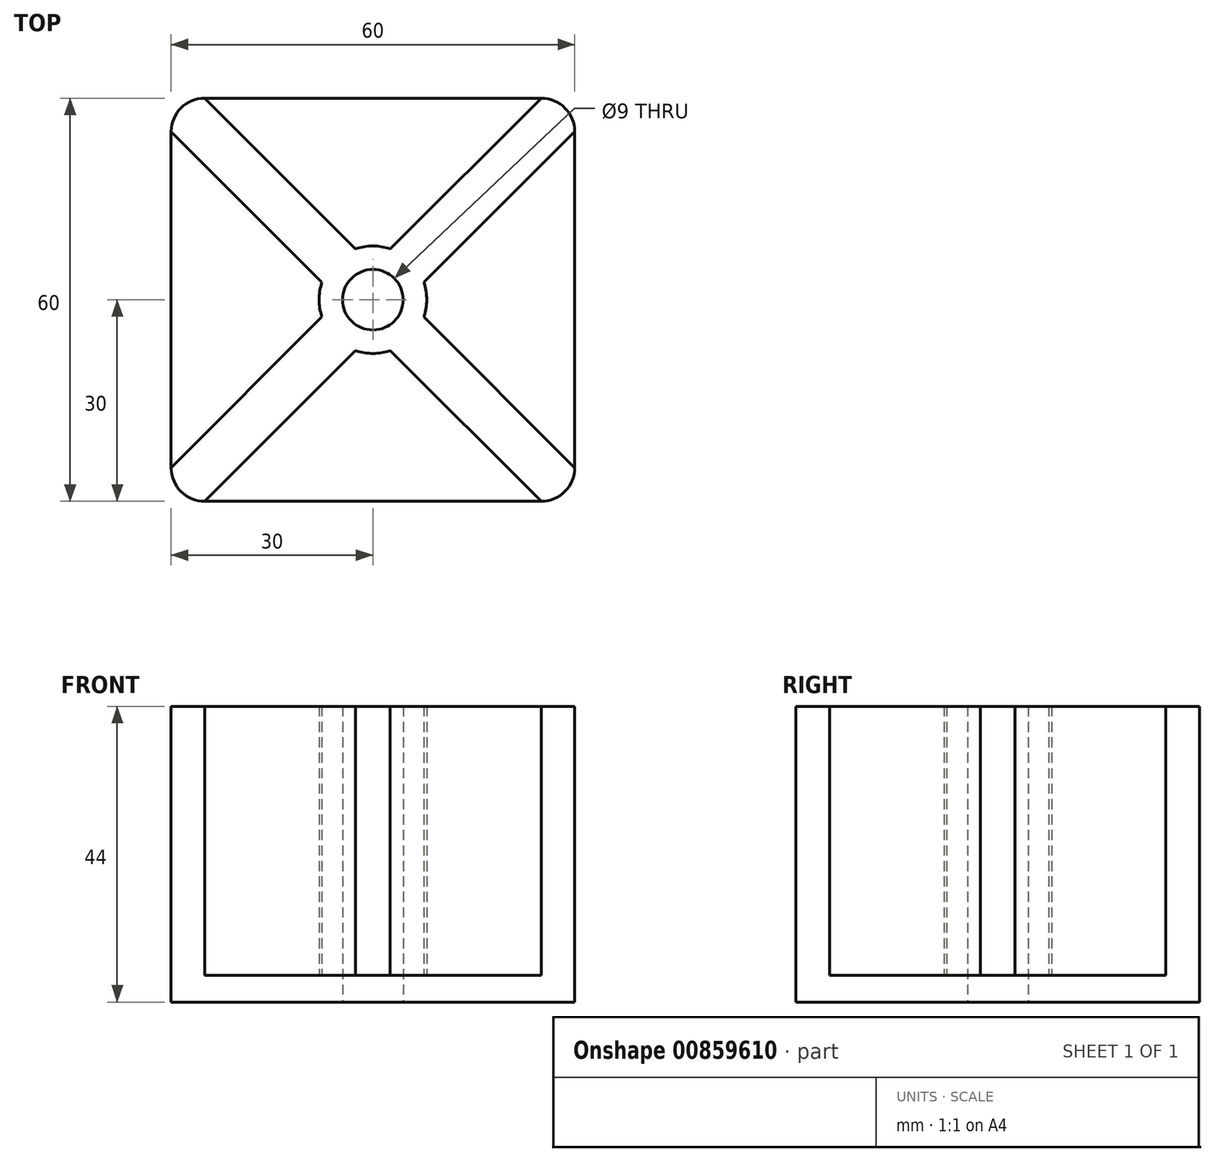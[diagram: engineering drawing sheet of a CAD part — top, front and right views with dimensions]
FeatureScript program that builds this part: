
annotation { "Feature Type Name" : "Feature", "Feature Type Description" : "" }
export const myFeature = defineFeature(function(context is Context, id is Id, definition is map)
    precondition{}
    {
        {
            var Q0;
            Q0=qCreatedBy(makeId("Top.planeOp"),FACE);
            var sketch = newSketch(context, id + "F0", { "sketchPlane" : qUnion([Q0])});
            skLineSegment(sketch, "E0.bottom", {"start": v(25, -30) * mm, "end": v(-25, -30) * mm});
            skLineSegment(sketch, "E0.top", {"start": v(25, 30) * mm, "end": v(-25, 30) * mm});
            skLineSegment(sketch, "E0.left", {"start": v(30, -25) * mm, "end": v(30, 25) * mm});
            skLineSegment(sketch, "E0.right", {"start": v(-30, -25) * mm, "end": v(-30, 25) * mm});
            skPoint(sketch, "E0.middle", {"position": v(0, 0) * mm});
            skPoint(sketch, "E1.visualSharp", {"position": v(30, 30) * mm});
            skArc(sketch, "E1.filletArc", {"start": v(30, 25) * mm, "mid": v(28.54, 28.54) * mm, "end": v(25, 30) * mm});
            skPoint(sketch, "E2.visualSharp", {"position": v(-30, 30) * mm});
            skArc(sketch, "E2.filletArc", {"start": v(-25, 30) * mm, "mid": v(-28.54, 28.54) * mm, "end": v(-30, 25) * mm});
            skPoint(sketch, "E3.visualSharp", {"position": v(-30, -30) * mm});
            skArc(sketch, "E3.filletArc", {"start": v(-30, -25) * mm, "mid": v(-28.54, -28.54) * mm, "end": v(-25, -30) * mm});
            skPoint(sketch, "E4.visualSharp", {"position": v(30, -30) * mm});
            skArc(sketch, "E4.filletArc", {"start": v(25, -30) * mm, "mid": v(28.54, -28.54) * mm, "end": v(30, -25) * mm});
            skSolve(sketch);
        }
        {
            var Q0;
            Q0 = qSketchRegion(id + "F0", true);
            extrude(context, id + "F1", {"entities" : qUnion([Q0]), "depth" : 4 * mm, "offsetDistance" : 25 * mm});
        }
        {
            var Q0;
            Q0=makeQuery(id+"F1.opExtrude","CAP_FACE",FACE,{"disambiguationData":[OSD([sQuery(id+"F0.wireOp",EDGE,"E0.bottom"),sQuery(id+"F0.wireOp",EDGE,"E0.top"),sQuery(id+"F0.wireOp",EDGE,"E0.left"),sQuery(id+"F0.wireOp",EDGE,"E0.right"),sQuery(id+"F0.wireOp",EDGE,"E1.filletArc"),sQuery(id+"F0.wireOp",EDGE,"E2.filletArc"),sQuery(id+"F0.wireOp",EDGE,"E3.filletArc"),sQuery(id+"F0.wireOp",EDGE,"E4.filletArc")])],"isStart":false});
            var sketch = newSketch(context, id + "F2", { "sketchPlane" : qUnion([Q0])});
            skCircle(sketch, "E5", {"center": v(0, 0) * mm, "radius": 4.5 * mm});
            skArc(sketch, "E6", {"start": v(-7.57, 2.57) * mm, "mid": v(-8, 0) * mm, "end": v(-7.57, -2.57) * mm});
            skLineSegment(sketch, "E7", {"start": v(-25, 30) * mm, "end": v(-2.57, 7.57) * mm});
            skLineSegment(sketch, "E8", {"start": v(-30, 25) * mm, "end": v(-7.57, 2.57) * mm});
            skLineSegment(sketch, "E9", {"start": v(-30, -25) * mm, "end": v(-7.57, -2.57) * mm});
            skLineSegment(sketch, "E10", {"start": v(-25, -30) * mm, "end": v(-2.57, -7.57) * mm});
            skLineSegment(sketch, "E11.trimOffspring", {"start": v(2.57, -7.57) * mm, "end": v(25, -30) * mm});
            skLineSegment(sketch, "E12.trimOffspring", {"start": v(2.57, 7.57) * mm, "end": v(25, 30) * mm});
            skLineSegment(sketch, "E13.trimOffspring", {"start": v(7.57, -2.57) * mm, "end": v(30, -25) * mm});
            skLineSegment(sketch, "E14.trimOffspring", {"start": v(7.57, 2.57) * mm, "end": v(30, 25) * mm});
            skArc(sketch, "E15.trimOffspring", {"start": v(2.57, 7.57) * mm, "mid": v(0, 8) * mm, "end": v(-2.57, 7.57) * mm});
            skArc(sketch, "E16.trimOffspring", {"start": v(7.57, -2.57) * mm, "mid": v(8, 0) * mm, "end": v(7.57, 2.57) * mm});
            skArc(sketch, "E17.trimOffspring", {"start": v(-2.57, -7.57) * mm, "mid": v(0, -8) * mm, "end": v(2.57, -7.57) * mm});
            skSolve(sketch);
        }
        {
            var Q0;
            Q0=makeQuery(id+"F2.imprint","IMPRINT",FACE,{"disambiguationData":[TD([[makeQuery(id+"F2.imprint","IMPRINT",EDGE,{"derivedFrom":sQuery(id+"F2.wireOp",EDGE,"E5")}),-1.0]])]});
            extrude(context, id + "F3", {"entities" : qUnion([Q0]), "operationType" : NewBodyOperationType.ADD, "depth" : 40 * mm, "offsetDistance" : 25 * mm});
        }
        {
            var Q0;
            Q0=makeQuery(id+"F2.imprint","IMPRINT",FACE,{"disambiguationData":[TD([[makeQuery(id+"F2.imprint","IMPRINT",EDGE,{"derivedFrom":sQuery(id+"F2.wireOp",EDGE,"E5")}),1.0]])]});
            extrude(context, id + "F4", {"entities" : qUnion([Q0]), "operationType" : NewBodyOperationType.REMOVE, "oppositeDirection" : true, "depth" : 25 * mm, "offsetDistance" : 25 * mm});
        }
    });
